# Revit family: MT
name_source: partatom
category: Lighting Fixtures
units: mm (PartAtom-declared; Revit-internal decimal feet)

## family parameters
Always vertical = Yes
Cut with Voids When Loaded = No
Light Source = Yes
Maintain Annotation Orientation = No
OmniClass Number = 23.80.70.00
OmniClass Title = Lighting
Part Type = Normal
Room Calculation Point = No
Round Connector Dimension = Use Diameter
Shared = No
Work Plane-Based = No

## types (5) — shared parameters
CRI = 70
Color Filter = 16777215
Default Elevation = 0' - 0"
Dimming Lamp Color Temperature Shift = <None>
Input Voltage = 120-277V
Lamp = LED
Load Classification = Lighting
Manufacturer = Above All Lighting
Power Factor = 0.9
Tilt Angle = 90.00°
URL = https://www.abovealllighting.com

## per-type parameters (varying)
| type | Model | Photometric Web File | Wattage Comments |
| MT-100W-4000K-IV | MT100401-IV | MT100401-IV_IESNA2002.IES | 100W |
| MT-150W-4000K-IV | MT150401-IV | MT150401-IV_IESNA2002.IES | 150W |
| MT-150W-4000K-VW | MT150401-VW | MT150401-VW_IESNA95.IES | 150W |
| MT-150W-4000K-VM | MT150401-VM | MT150401-VM_IESNA2002.IES | 150W |
| MT-150W-4000K-III | MT150401-III | MT150401-III_IESNA2002.IES | 150W |

## geometry (parser evidence)
native form markers: Sweep x5
no freeform markers — native parametric forms only
